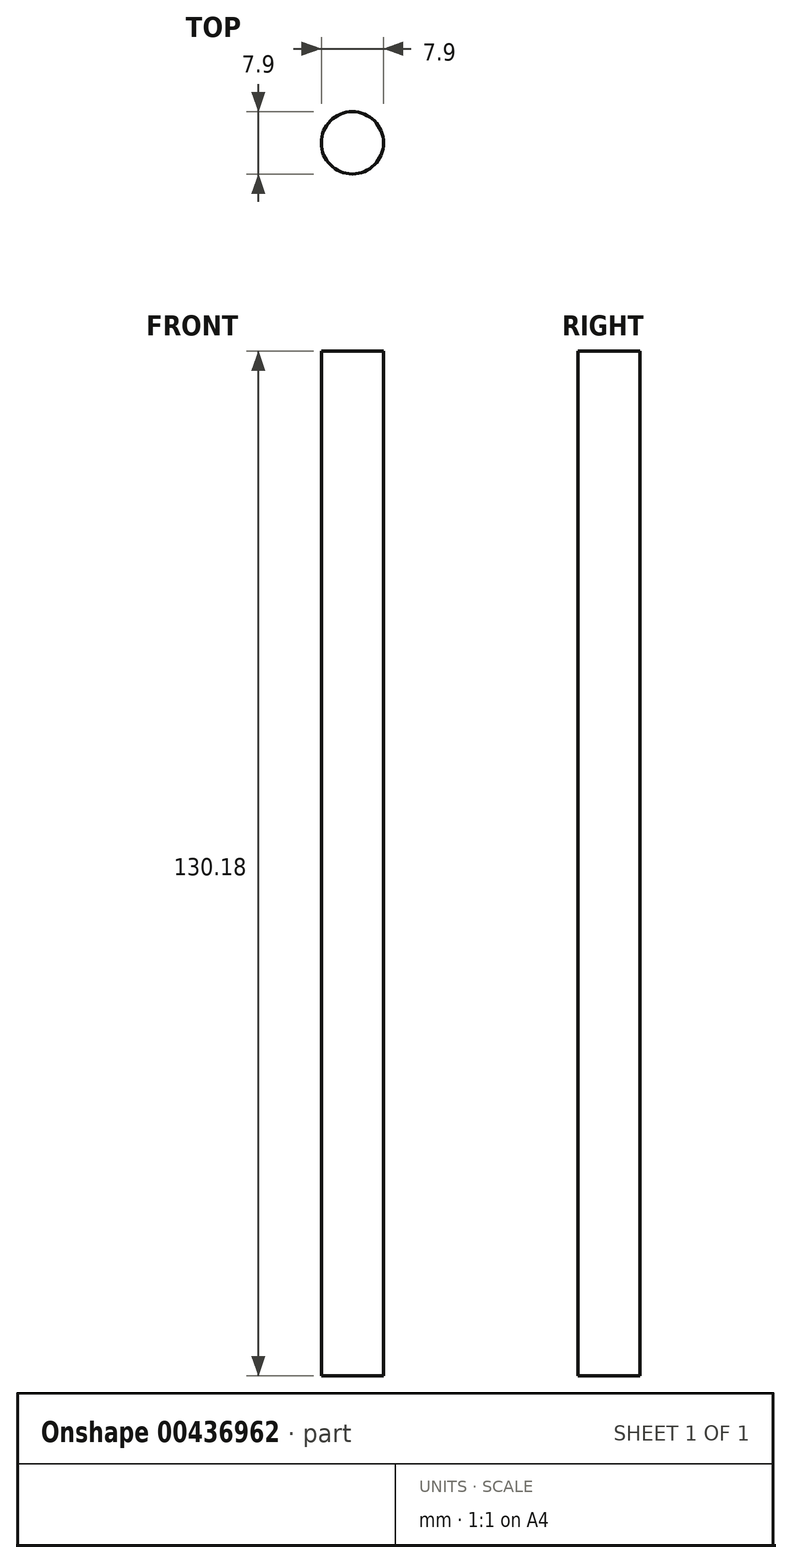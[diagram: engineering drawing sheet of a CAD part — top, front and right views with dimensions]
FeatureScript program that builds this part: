
annotation { "Feature Type Name" : "Feature", "Feature Type Description" : "" }
export const myFeature = defineFeature(function(context is Context, id is Id, definition is map)
    precondition{}
    {
        {
            var Q0;
            Q0=qCreatedBy(makeId("Top.planeOp"),FACE);
            var sketch = newSketch(context, id + "F0", { "sketchPlane" : qUnion([Q0])});
            skCircle(sketch, "E0", {"center": v(0, 0) * mm, "radius": 3.95 * mm});
            skSolve(sketch);
        }
        {
            var Q0;
            Q0=qSketchRegion(id+"F0",true);
            extrude(context, id + "F1", {"entities" : qUnion([Q0]), "depth" : 130.17 * mm});
        }
    });
